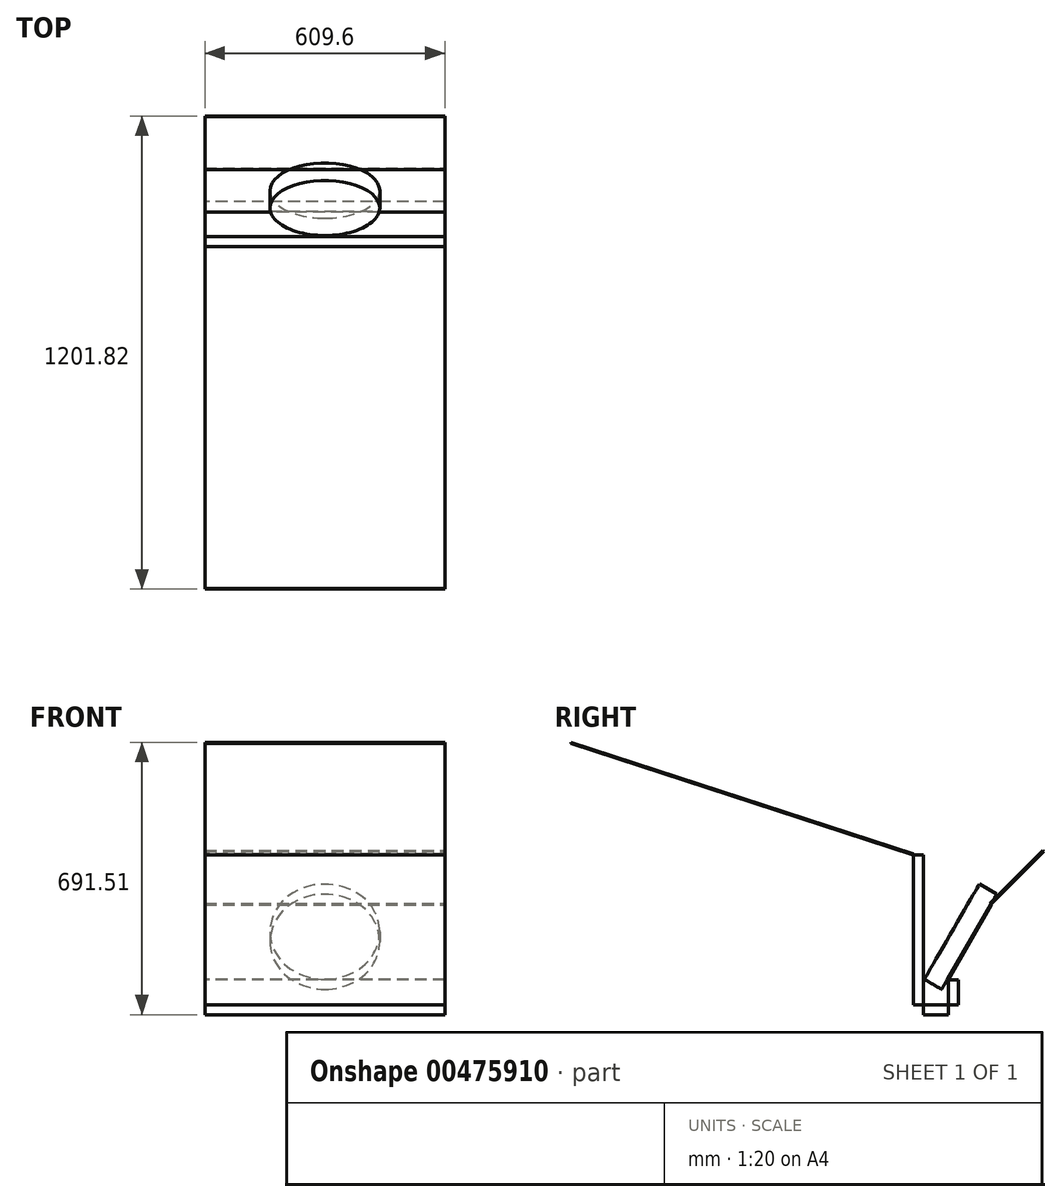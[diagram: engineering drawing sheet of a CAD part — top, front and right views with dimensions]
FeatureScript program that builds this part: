
annotation { "Feature Type Name" : "Feature", "Feature Type Description" : "" }
export const myFeature = defineFeature(function(context is Context, id is Id, definition is map)
    precondition{}
    {
        {
            var Q0;
            Q0=qCreatedBy(makeId("Front.planeOp"),FACE);
            var sketch = newSketch(context, id + "F0", { "sketchPlane" : qUnion([Q0])});
            skLineSegment(sketch, "E0.bottom", {"start": v(304.8, 200.25) * mm, "end": v(-304.8, 200.25) * mm});
            skLineSegment(sketch, "E0.top", {"start": v(304.8, -180.75) * mm, "end": v(-304.8, -180.75) * mm});
            skLineSegment(sketch, "E0.left", {"start": v(304.8, 200.25) * mm, "end": v(304.8, -180.75) * mm});
            skLineSegment(sketch, "E0.right", {"start": v(-304.8, 200.25) * mm, "end": v(-304.8, -180.75) * mm});
            skPoint(sketch, "E0.middle", {"position": v(0, 9.75) * mm});
            skSolve(sketch);
        }
        {
            var Q0;
            Q0 = qSketchRegion(id + "F0", true);
            extrude(context, id + "F1", {"entities" : qUnion([Q0]), "depth" : 25.4 * mm, "offsetDistance" : 25.4 * mm});
        }
        {
            var Q0;
            Q0=makeQuery(id+"F1.opExtrude","SWEPT_FACE",FACE,{"disambiguationData":[OSD([sQuery(id+"F0.wireOp",EDGE,"E0.top")])]});
            var sketch = newSketch(context, id + "F2", { "sketchPlane" : qUnion([Q0])});
            skLineSegment(sketch, "E1.bottom", {"start": v(-304.8, 0) * mm, "end": v(304.8, 0) * mm});
            skLineSegment(sketch, "E1.top", {"start": v(-304.8, -63.5) * mm, "end": v(304.8, -63.5) * mm});
            skLineSegment(sketch, "E1.left", {"start": v(-304.8, 0) * mm, "end": v(-304.8, -63.5) * mm});
            skLineSegment(sketch, "E1.right", {"start": v(304.8, 0) * mm, "end": v(304.8, -63.5) * mm});
            skSolve(sketch);
        }
        {
            var Q0;
            Q0 = qSketchRegion(id + "F2", true);
            extrude(context, id + "F3", {"entities" : qUnion([Q0]), "depth" : 25.4 * mm, "offsetDistance" : 25.4 * mm});
        }
        {
            var Q0;
            Q0=makeQuery(id+"F3.opExtrude","SWEPT_FACE",FACE,{"disambiguationData":[OSD([sQuery(id+"F2.wireOp",EDGE,"E1.top")])]});
            var sketch = newSketch(context, id + "F4", { "sketchPlane" : qUnion([Q0])});
            skLineSegment(sketch, "E2.bottom", {"start": v(-304.8, -117.25) * mm, "end": v(304.8, -117.25) * mm});
            skLineSegment(sketch, "E2.top", {"start": v(-304.8, -180.75) * mm, "end": v(304.8, -180.75) * mm});
            skLineSegment(sketch, "E2.left", {"start": v(-304.8, -117.25) * mm, "end": v(-304.8, -180.75) * mm});
            skLineSegment(sketch, "E2.right", {"start": v(304.8, -117.25) * mm, "end": v(304.8, -180.75) * mm});
            skSolve(sketch);
        }
        {
            var Q0;
            Q0 = qSketchRegion(id + "F4", true);
            extrude(context, id + "F5", {"entities" : qUnion([Q0]), "depth" : 25.4 * mm, "offsetDistance" : 25.4 * mm});
        }
        {
            var Q0;
            Q0=makeQuery(id+"F5.opExtrude","CAP_FACE",FACE,{"disambiguationData":[OSD([sQuery(id+"F4.wireOp",EDGE,"E2.bottom"),sQuery(id+"F4.wireOp",EDGE,"E2.top"),sQuery(id+"F4.wireOp",EDGE,"E2.left"),sQuery(id+"F4.wireOp",EDGE,"E2.right")])],"isStart":true});
            var sketch = newSketch(context, id + "F6", { "sketchPlane" : qUnion([Q0])});
            skLineSegment(sketch, "E3.bottom", {"start": v(-304.8, -117.25) * mm, "end": v(304.8, -117.25) * mm});
            skLineSegment(sketch, "E3.top", {"start": v(-304.8, 102.72) * mm, "end": v(304.8, 102.72) * mm});
            skLineSegment(sketch, "E3.left", {"start": v(-304.8, -117.25) * mm, "end": v(-304.8, 102.72) * mm});
            skLineSegment(sketch, "E3.right", {"start": v(304.8, -117.25) * mm, "end": v(304.8, 102.72) * mm});
            skSolve(sketch);
        }
        {
            var Q0;
            Q0 = qSketchRegion(id + "F6", true);
            extrude(context, id + "F7", {"entities" : qUnion([Q0]), "depth" : 2.54 * mm, "offsetDistance" : 25.4 * mm});
        }
        {
            var Q0;
            Q0=makeQuery(id+"F7.opExtrude","SWEPT_BODY",BODY,{"disambiguationData":[OSD([sQuery(id+"F6.wireOp",EDGE,"E3.bottom"),sQuery(id+"F6.wireOp",EDGE,"E3.top"),sQuery(id+"F6.wireOp",EDGE,"E3.left"),sQuery(id+"F6.wireOp",EDGE,"E3.right")])]});
            var Q1;
            Q1=makeQuery(id+"F5.opExtrude","CAP_EDGE",EDGE,{"disambiguationData":[OSD([sQuery(id+"F4.wireOp",EDGE,"E2.bottom")])],"isStart":true});
            transform(context, id + "F8", {"entities" : qUnion([Q0]), "transformType" : TransformType.ROTATION, "transformAxis" : qUnion([Q1]), "angle" : 30 * degree, "makeCopy" : false});
        }
        {
            var Q0;
            Q0=makeQuery(id+"F7.opExtrude","CAP_FACE",FACE,{"disambiguationData":[OSD([sQuery(id+"F6.wireOp",EDGE,"E3.bottom"),sQuery(id+"F6.wireOp",EDGE,"E3.top"),sQuery(id+"F6.wireOp",EDGE,"E3.left"),sQuery(id+"F6.wireOp",EDGE,"E3.right")])],"isStart":false});
            var sketch = newSketch(context, id + "F9", { "sketchPlane" : qUnion([Q0])});
            skLineSegment(sketch, "E4.bottom", {"start": v(-304.8, 340.67) * mm, "end": v(304.8, 340.67) * mm});
            skLineSegment(sketch, "E4.top", {"start": v(-304.8, 150.17) * mm, "end": v(304.8, 150.17) * mm});
            skLineSegment(sketch, "E4.left", {"start": v(-304.8, 150.17) * mm, "end": v(-304.8, 340.67) * mm});
            skLineSegment(sketch, "E4.right", {"start": v(304.8, 150.17) * mm, "end": v(304.8, 340.67) * mm});
            skSolve(sketch);
        }
        {
            var Q0;
            Q0=makeQuery(id+"F9.imprint","IMPRINT",FACE,{"disambiguationData":[TD([[makeQuery(id+"F9.imprint","IMPRINT",EDGE,{"derivedFrom":sQuery(id+"F9.wireOp",EDGE,"E4.bottom")}),-1.0]])]});
            extrude(context, id + "F10", {"entities" : qUnion([Q0]), "depth" : 2.54 * mm, "offsetDistance" : 25.4 * mm});
        }
        {
            var Q0;
            Q0=makeQuery(id+"F10.opExtrude","SWEPT_BODY",BODY,{"disambiguationData":[OSD([sQuery(id+"F9.wireOp",EDGE,"E4.bottom"),sQuery(id+"F9.wireOp",EDGE,"E4.top"),sQuery(id+"F9.wireOp",EDGE,"E4.left"),sQuery(id+"F9.wireOp",EDGE,"E4.right")])]});
            var Q1;
            Q1=makeQuery(id+"F7.opExtrude","CAP_EDGE",EDGE,{"disambiguationData":[OSD([sQuery(id+"F6.wireOp",EDGE,"E3.top")])],"isStart":false});
            transform(context, id + "F11", {"entities" : qUnion([Q0]), "transformType" : TransformType.ROTATION, "transformAxis" : qUnion([Q1]), "angle" : 15 * degree, "oppositeDirection" : true, "makeCopy" : false});
        }
        {
            var Q0;
            Q0=makeQuery(id+"F7.opExtrude","CAP_FACE",FACE,{"disambiguationData":[OSD([sQuery(id+"F6.wireOp",EDGE,"E3.bottom"),sQuery(id+"F6.wireOp",EDGE,"E3.top"),sQuery(id+"F6.wireOp",EDGE,"E3.left"),sQuery(id+"F6.wireOp",EDGE,"E3.right")])],"isStart":false});
            var sketch = newSketch(context, id + "F12", { "sketchPlane" : qUnion([Q0])});
            skCircle(sketch, "E5", {"center": v(0, 40.2) * mm, "radius": 139.7 * mm});
            skPoint(sketch, "E6", {"position": v(0, 150.17) * mm});
            skLineSegment(sketch, "E7", {"start": v(0, 150.17) * mm, "end": v(0, -69.79) * mm});
            skSolve(sketch);
        }
        {
            var Q0;
            Q0 = qSketchRegion(id + "F12", true);
            extrude(context, id + "F13", {"entities" : qUnion([Q0]), "depth" : 50.8 * mm, "offsetDistance" : 25.4 * mm});
        }
        {
            var Q0;
            Q0=makeQuery(id+"F1.opExtrude","SWEPT_FACE",FACE,{"disambiguationData":[OSD([sQuery(id+"F0.wireOp",EDGE,"E0.bottom")])]});
            var sketch = newSketch(context, id + "F14", { "sketchPlane" : qUnion([Q0])});
            skLineSegment(sketch, "E8.bottom", {"start": v(-304.8, -939.8) * mm, "end": v(304.8, -939.8) * mm});
            skLineSegment(sketch, "E8.top", {"start": v(-304.8, -25.4) * mm, "end": v(304.8, -25.4) * mm});
            skLineSegment(sketch, "E8.left", {"start": v(-304.8, -939.8) * mm, "end": v(-304.8, -25.4) * mm});
            skLineSegment(sketch, "E8.right", {"start": v(304.8, -939.8) * mm, "end": v(304.8, -25.4) * mm});
            skSolve(sketch);
        }
        {
            var Q0;
            Q0 = qSketchRegion(id + "F14", true);
            extrude(context, id + "F15", {"entities" : qUnion([Q0]), "depth" : 2.54 * mm, "offsetDistance" : 25.4 * mm});
        }
        {
            var Q0;
            Q0=makeQuery(id+"F15.opExtrude","SWEPT_BODY",BODY,{"disambiguationData":[OSD([sQuery(id+"F14.wireOp",EDGE,"E8.bottom"),sQuery(id+"F14.wireOp",EDGE,"E8.top"),sQuery(id+"F14.wireOp",EDGE,"E8.left"),sQuery(id+"F14.wireOp",EDGE,"E8.right")])]});
            var Q1;
            Q1=makeQuery(id+"F15.opExtrude","CAP_EDGE",EDGE,{"disambiguationData":[OSD([sQuery(id+"F14.wireOp",EDGE,"E8.top")])],"isStart":false});
            transform(context, id + "F16", {"entities" : qUnion([Q0]), "transformType" : TransformType.ROTATION, "transformAxis" : qUnion([Q1]), "angle" : 18 * degree, "makeCopy" : false});
        }
    });
